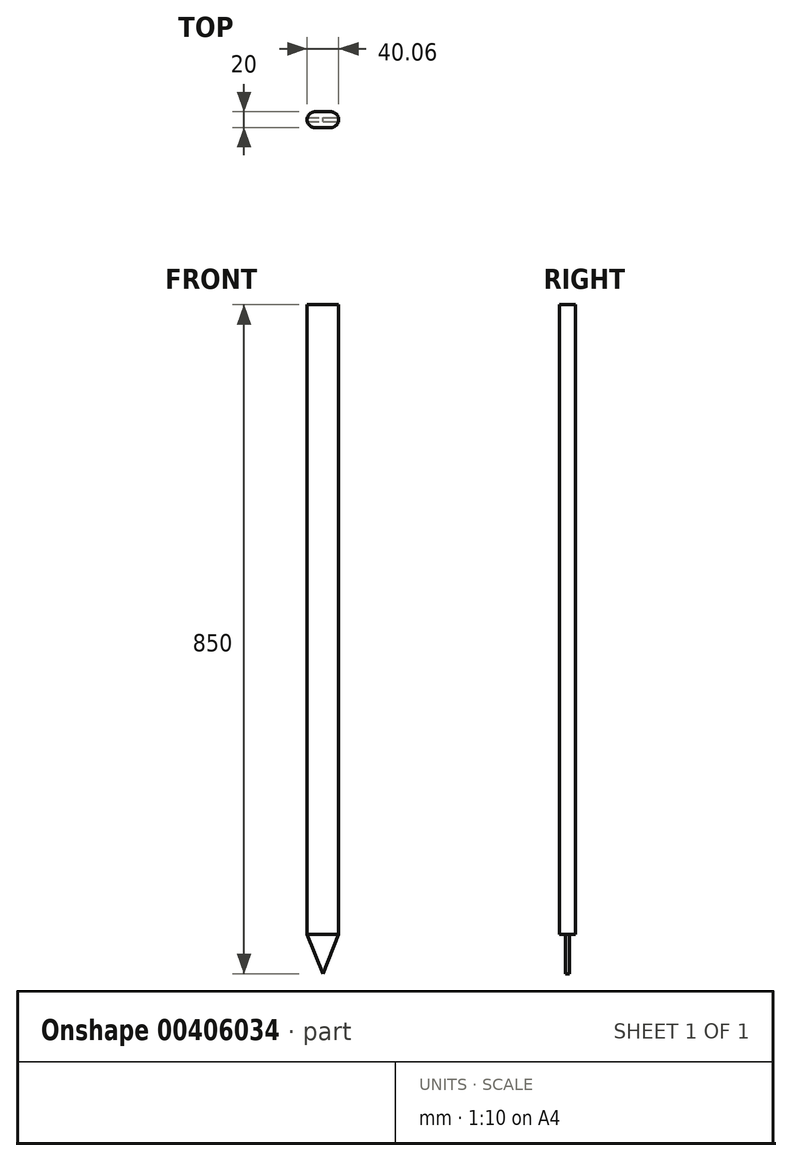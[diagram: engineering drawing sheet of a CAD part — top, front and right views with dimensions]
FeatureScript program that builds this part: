
annotation { "Feature Type Name" : "Feature", "Feature Type Description" : "" }
export const myFeature = defineFeature(function(context is Context, id is Id, definition is map)
    precondition{}
    {
        {
            var Q0;
            Q0=qCreatedBy(makeId("Top.planeOp"),FACE);
            var sketch = newSketch(context, id + "F0", { "sketchPlane" : qUnion([Q0])});
            skLineSegment(sketch, "E0.bottom", {"start": v(-20, 10) * mm, "end": v(20, 10) * mm});
            skLineSegment(sketch, "E0.top", {"start": v(-20, -10) * mm, "end": v(20, -10) * mm});
            skLineSegment(sketch, "E0.left", {"start": v(-20, 10) * mm, "end": v(-20, -10) * mm});
            skLineSegment(sketch, "E0.right", {"start": v(20, 10) * mm, "end": v(20, -10) * mm});
            skPoint(sketch, "E0.middle", {"position": v(0, 0) * mm});
            skSolve(sketch);
        }
        {
            var Q0;
            Q0=makeQuery(id+"F0.imprint","IMPRINT",FACE,{"disambiguationData":[TD([[makeQuery(id+"F0.imprint","IMPRINT",EDGE,{"derivedFrom":sQuery(id+"F0.wireOp",EDGE,"E0.bottom")}),-1.0]])]});
            extrude(context, id + "F1", {"entities" : qUnion([Q0]), "depth" : 800 * mm});
        }
        {
            var Q0;
            Q0=makeQuery(id+"F1.opExtrude","SWEPT_EDGE",EDGE,{"disambiguationData":[OSD([sQuery(id+"F0.wireOp",EDGE,"E0.top"),sQuery(id+"F0.wireOp",EDGE,"E0.right")])]});
            var Q1;
            Q1=makeQuery(id+"F1.opExtrude","SWEPT_EDGE",EDGE,{"disambiguationData":[OSD([sQuery(id+"F0.wireOp",EDGE,"E0.bottom"),sQuery(id+"F0.wireOp",EDGE,"E0.right")])]});
            var Q2;
            Q2=makeQuery(id+"F1.opExtrude","SWEPT_EDGE",EDGE,{"disambiguationData":[OSD([sQuery(id+"F0.wireOp",EDGE,"E0.top"),sQuery(id+"F0.wireOp",EDGE,"E0.left")])]});
            var Q3;
            Q3=makeQuery(id+"F1.opExtrude","SWEPT_EDGE",EDGE,{"disambiguationData":[OSD([sQuery(id+"F0.wireOp",EDGE,"E0.bottom"),sQuery(id+"F0.wireOp",EDGE,"E0.left")])]});
            fillet(context, id + "F2", {"entities" : qUnion([Q0, Q1, Q2, Q3]), "radius" : 10 * mm, "tangentPropagation" : true, "allowEdgeOverflow" : false});
        }
        {
            var Q0;
            Q0=qCreatedBy(makeId("Front.planeOp"),FACE);
            var sketch = newSketch(context, id + "F3", { "sketchPlane" : qUnion([Q0])});
            skLineSegment(sketch, "E1", {"start": v(-20.06, 0) * mm, "end": v(0, -50) * mm});
            skLineSegment(sketch, "E2", {"start": v(0, -50) * mm, "end": v(19.94, 0) * mm});
            skLineSegment(sketch, "E3", {"start": v(-20.06, 0) * mm, "end": v(19.94, 0) * mm});
            skSolve(sketch);
        }
        {
            var Q0;
            Q0=makeQuery(id+"F3.imprint","IMPRINT",FACE,{"disambiguationData":[TD([[makeQuery(id+"F3.imprint","IMPRINT",EDGE,{"derivedFrom":sQuery(id+"F3.wireOp",EDGE,"E1")}),1.0]])]});
            extrude(context, id + "F4", {"entities" : qUnion([Q0]), "operationType" : NewBodyOperationType.ADD, "endBound" : BoundingType.SYMMETRIC, "depth" : 5 * mm});
        }
    });
